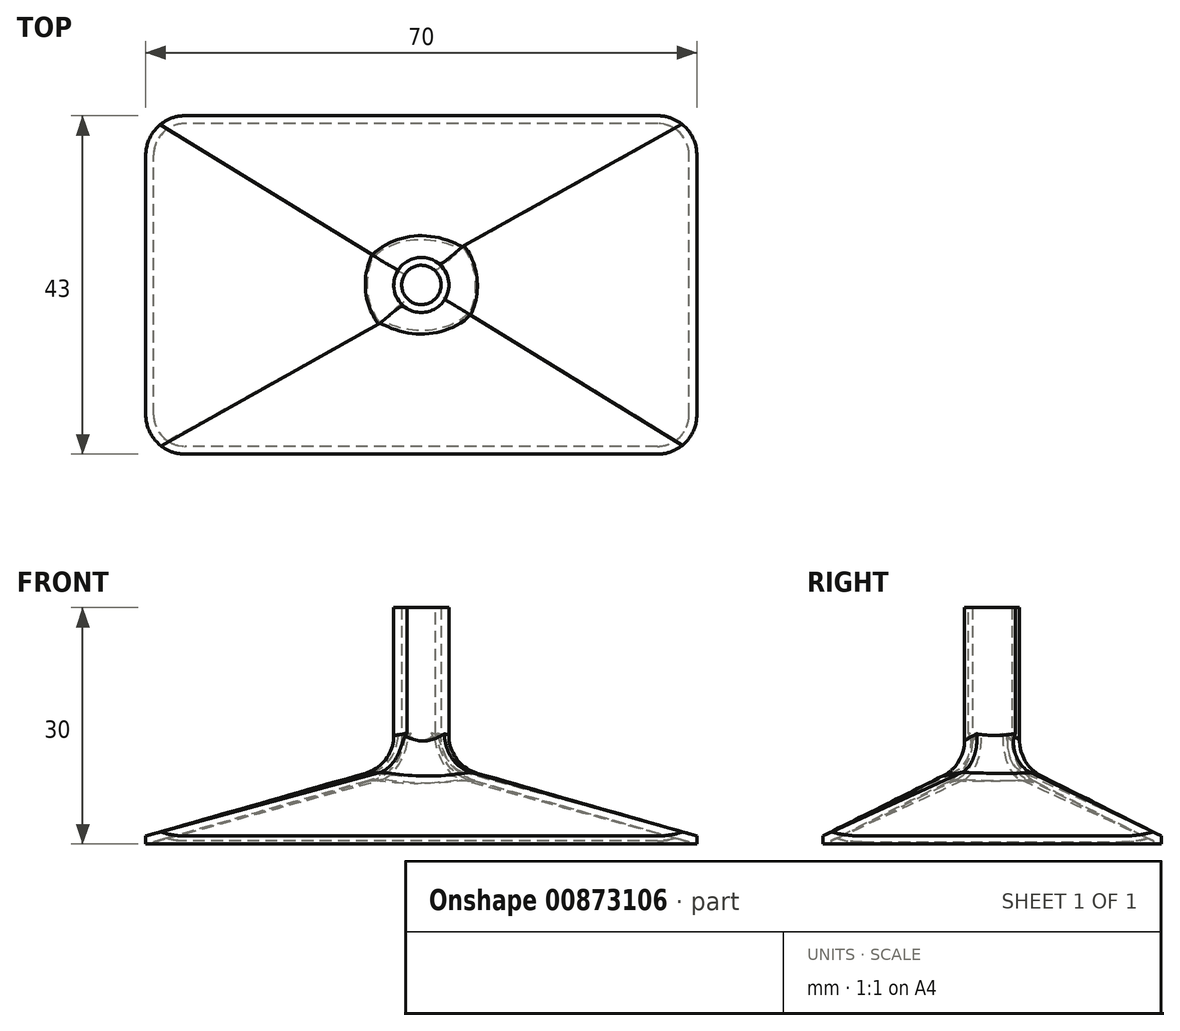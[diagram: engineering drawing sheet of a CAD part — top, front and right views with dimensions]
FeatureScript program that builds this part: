
annotation { "Feature Type Name" : "Feature", "Feature Type Description" : "" }
export const myFeature = defineFeature(function(context is Context, id is Id, definition is map)
    precondition{}
    {
        {
            var Q0;
            Q0=qCreatedBy(makeId("Top.planeOp"),FACE);
            var sketch = newSketch(context, id + "F0", { "sketchPlane" : qUnion([Q0])});
            skLineSegment(sketch, "E0.bottom", {"start": v(35, -21.5) * mm, "end": v(-35, -21.5) * mm});
            skLineSegment(sketch, "E0.top", {"start": v(35, 21.5) * mm, "end": v(-35, 21.5) * mm});
            skLineSegment(sketch, "E0.left", {"start": v(35, -21.5) * mm, "end": v(35, 21.5) * mm});
            skLineSegment(sketch, "E0.right", {"start": v(-35, -21.5) * mm, "end": v(-35, 21.5) * mm});
            skPoint(sketch, "E0.middle", {"position": v(0, 0) * mm});
            skSolve(sketch);
        }
        {
            var Q0;
            Q0=makeQuery(id+"F0.imprint","IMPRINT",FACE,{"disambiguationData":[TD([[makeQuery(id+"F0.imprint","IMPRINT",EDGE,{"derivedFrom":sQuery(id+"F0.wireOp",EDGE,"E0.bottom")}),-1.0]])]});
            extrude(context, id + "F1", {"entities" : qUnion([Q0]), "depth" : 1 * mm, "offsetDistance" : 25 * mm});
        }
        {
            var Q0;
            Q0=qCreatedBy(makeId("Top.planeOp"),FACE);
            cPlane(context, id + "F2", {"entities" : qUnion([Q0]), "cplaneType" : CPlaneType.OFFSET, "offset" : 10 * mm, "width" : 150 * mm, "height" : 150 * mm});
        }
        {
            var Q0;
            Q0=qCreatedBy(id+"F2.planeOp",FACE);
            var sketch = newSketch(context, id + "F3", { "sketchPlane" : qUnion([Q0])});
            skCircle(sketch, "E1", {"center": v(0, 0) * mm, "radius": 3.5 * mm});
            skSolve(sketch);
        }
        {
            var Q1;
            Q1=makeQuery(id+"F1.opExtrude","CAP_FACE",FACE,{"disambiguationData":[OSD([sQuery(id+"F0.wireOp",EDGE,"E0.bottom"),sQuery(id+"F0.wireOp",EDGE,"E0.top"),sQuery(id+"F0.wireOp",EDGE,"E0.left"),sQuery(id+"F0.wireOp",EDGE,"E0.right")])],"isStart":false});
            var Q2;
            Q2=makeQuery(id+"F3.imprint","IMPRINT",FACE,{"disambiguationData":[TD([[makeQuery(id+"F3.imprint","IMPRINT",EDGE,{"derivedFrom":sQuery(id+"F3.wireOp",EDGE,"E1")}),1.0]])]});
            loft(context, id + "F4", {"operationType" : NewBodyOperationType.ADD, "sheetProfilesArray" : [{ "sheetProfileEntities" : qUnion([Q1]) }, { "sheetProfileEntities" : qUnion([Q2]) }]});
        }
        {
            var Q0;
            Q0=makeQuery(id+"F4.opLoft","CAP_FACE",FACE,{"disambiguationData":[OSD([makeQuery(id+"F3.imprint","IMPRINT",FACE,{"disambiguationData":[TD([[makeQuery(id+"F3.imprint","IMPRINT",EDGE,{"derivedFrom":sQuery(id+"F3.wireOp",EDGE,"E1")}),1.0]])]})])],"isStart":true});
            var sketch = newSketch(context, id + "F5", { "sketchPlane" : qUnion([Q0])});
            skSolve(sketch);
        }
        {
            var Q0;
            {var subQ0=sQuery(id+"F3.wireOp",EDGE,"E1");var subQ2=sQuery(id+"F0.wireOp",EDGE,"E0.left");var subQ4=sQuery(id+"F0.wireOp",EDGE,"E0.bottom");Q0=makeQuery(id+"F5.imprint","IMPRINT",FACE,{"disambiguationData":[TD([[makeQuery(id+"F5.imprint","IMPRINT",EDGE,{"derivedFrom":makeQuery(id+"F4.opLoft","MID_CAP_EDGE",EDGE,{"disambiguationData":[OSD([subQ4,subQ2,subQ0])],"capPos":1.0})}),1.0]])]});}
            extrude(context, id + "F6", {"entities" : qUnion([Q0]), "operationType" : NewBodyOperationType.ADD, "depth" : 20 * mm, "offsetDistance" : 25 * mm});
        }
        {
            var Q0;
            Q0=makeQuery(id+"F1.opExtrude","SWEPT_EDGE",EDGE,{"disambiguationData":[OSD([sQuery(id+"F0.wireOp",EDGE,"E0.bottom"),sQuery(id+"F0.wireOp",EDGE,"E0.left")])]});
            var Q1;
            Q1=makeQuery(id+"F1.opExtrude","SWEPT_EDGE",EDGE,{"disambiguationData":[OSD([sQuery(id+"F0.wireOp",EDGE,"E0.top"),sQuery(id+"F0.wireOp",EDGE,"E0.left")])]});
            var Q2;
            Q2=makeQuery(id+"F1.opExtrude","SWEPT_EDGE",EDGE,{"disambiguationData":[OSD([sQuery(id+"F0.wireOp",EDGE,"E0.bottom"),sQuery(id+"F0.wireOp",EDGE,"E0.right")])]});
            var Q3;
            Q3=makeQuery(id+"F1.opExtrude","SWEPT_EDGE",EDGE,{"disambiguationData":[OSD([sQuery(id+"F0.wireOp",EDGE,"E0.top"),sQuery(id+"F0.wireOp",EDGE,"E0.right")])]});
            var Q4;
            {var subQ0=sQuery(id+"F3.wireOp",EDGE,"E1");var subQ1=sQuery(id+"F0.wireOp",EDGE,"E0.right");var subQ2=sQuery(id+"F0.wireOp",EDGE,"E0.left");var subQ3=sQuery(id+"F0.wireOp",EDGE,"E0.top");var subQ4=sQuery(id+"F0.wireOp",EDGE,"E0.bottom");Q4=makeQuery(id+"F6.boolean.opBoolean","MERGE",EDGE,{"derivedFrom":[makeQuery(id+"F4.opLoft","MID_CAP_EDGE",EDGE,{"disambiguationData":[OSD([subQ4,subQ3,subQ2,subQ1,subQ0])],"capPos":1.0}),makeQuery(id+"F6.opExtrude","CAP_EDGE",EDGE,{"disambiguationData":[OSD([subQ4,subQ3,subQ2,subQ1,subQ0])],"isStart":true})]});}
            var Q5;
            {var subQ0=sQuery(id+"F3.wireOp",EDGE,"E1");var subQ1=sQuery(id+"F0.wireOp",EDGE,"E0.right");var subQ2=sQuery(id+"F0.wireOp",EDGE,"E0.left");var subQ3=sQuery(id+"F0.wireOp",EDGE,"E0.top");Q5=makeQuery(id+"F6.boolean.opBoolean","MERGE",EDGE,{"derivedFrom":[makeQuery(id+"F4.opLoft","MID_CAP_EDGE",EDGE,{"disambiguationData":[OSD([subQ3,subQ2,subQ1,subQ0])],"capPos":1.0}),makeQuery(id+"F6.opExtrude","CAP_EDGE",EDGE,{"disambiguationData":[OSD([subQ3,subQ2,subQ1,subQ0])],"isStart":true})]});}
            var Q6;
            {var subQ0=sQuery(id+"F3.wireOp",EDGE,"E1");var subQ1=sQuery(id+"F0.wireOp",EDGE,"E0.left");var subQ2=sQuery(id+"F0.wireOp",EDGE,"E0.bottom");Q6=makeQuery(id+"F6.boolean.opBoolean","MERGE",EDGE,{"derivedFrom":[makeQuery(id+"F4.opLoft","MID_CAP_EDGE",EDGE,{"disambiguationData":[OSD([subQ2,subQ1,subQ0])],"capPos":1.0}),makeQuery(id+"F6.opExtrude","CAP_EDGE",EDGE,{"disambiguationData":[OSD([subQ2,subQ1,subQ0])],"isStart":true})]});}
            var Q7;
            {var subQ0=sQuery(id+"F3.wireOp",EDGE,"E1");var subQ1=sQuery(id+"F0.wireOp",EDGE,"E0.left");var subQ2=sQuery(id+"F0.wireOp",EDGE,"E0.top");var subQ3=sQuery(id+"F0.wireOp",EDGE,"E0.bottom");Q7=makeQuery(id+"F6.boolean.opBoolean","MERGE",EDGE,{"derivedFrom":[makeQuery(id+"F4.opLoft","MID_CAP_EDGE",EDGE,{"disambiguationData":[OSD([subQ3,subQ2,subQ1,subQ0])],"capPos":1.0}),makeQuery(id+"F6.opExtrude","CAP_EDGE",EDGE,{"disambiguationData":[OSD([subQ3,subQ2,subQ1,subQ0])],"isStart":true})]});}
            fillet(context, id + "F7", {"entities" : qUnion([Q0, Q1, Q2, Q3, Q4, Q5, Q6, Q7]), "radius" : 5 * mm, "tangentPropagation" : true, "allowEdgeOverflow" : false});
        }
        {
            var Q0;
            Q0=makeQuery(id+"F1.opExtrude","CAP_FACE",FACE,{"disambiguationData":[OSD([sQuery(id+"F0.wireOp",EDGE,"E0.bottom"),sQuery(id+"F0.wireOp",EDGE,"E0.top"),sQuery(id+"F0.wireOp",EDGE,"E0.left"),sQuery(id+"F0.wireOp",EDGE,"E0.right")])],"isStart":true});
            var Q1;
            Q1=makeQuery(id+"F6.opExtrude","CAP_FACE",FACE,{"disambiguationData":[OSD([sQuery(id+"F0.wireOp",EDGE,"E0.bottom"),sQuery(id+"F0.wireOp",EDGE,"E0.top"),sQuery(id+"F0.wireOp",EDGE,"E0.left"),sQuery(id+"F0.wireOp",EDGE,"E0.right"),sQuery(id+"F3.wireOp",EDGE,"E1")])],"isStart":false});
            shell(context, id + "F8", {"entities" : qUnion([Q0, Q1]), "thickness" : 1 * mm});
        }
    });
